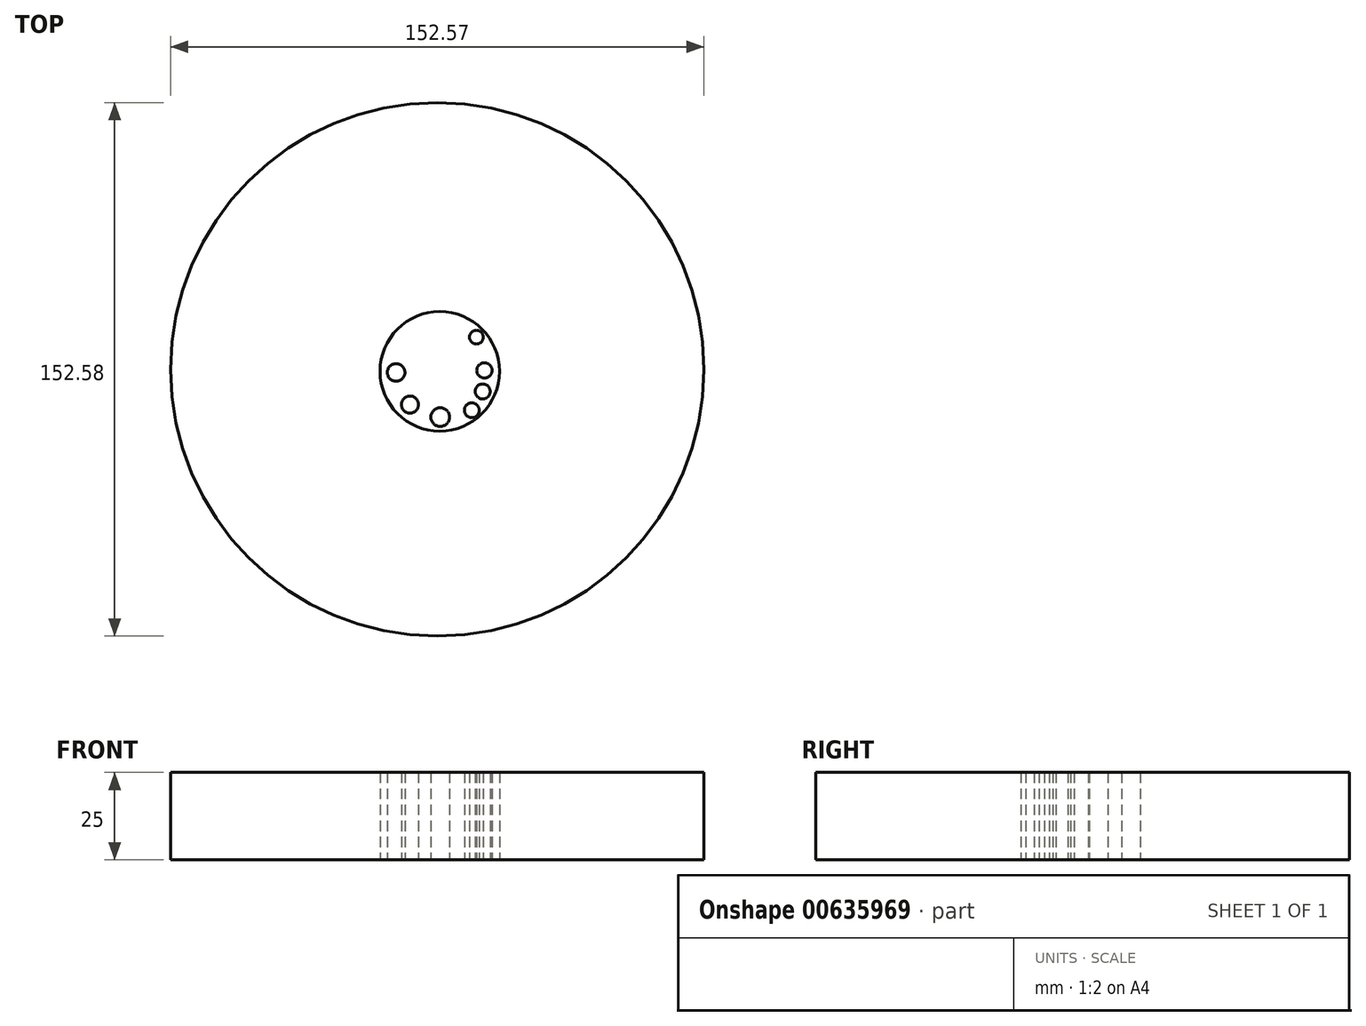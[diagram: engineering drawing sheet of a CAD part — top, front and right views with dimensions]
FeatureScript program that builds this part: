
annotation { "Feature Type Name" : "Feature", "Feature Type Description" : "" }
export const myFeature = defineFeature(function(context is Context, id is Id, definition is map)
    precondition{}
    {
        {
            var Q0;
            Q0=qCreatedBy(makeId("Top.planeOp"),FACE);
            var sketch = newSketch(context, id + "F0", { "sketchPlane" : qUnion([Q0])});
            skCircle(sketch, "E0", {"center": v(0, 0) * mm, "radius": 17.1 * mm});
            skSolve(sketch);
        }
        {
            var Q0;
            Q0=qCreatedBy(makeId("Top.planeOp"),FACE);
            var sketch = newSketch(context, id + "F1", { "sketchPlane" : qUnion([Q0])});
            skLineSegment(sketch, "E1", {"start": v(-13.82, 9.06) * mm, "end": v(-63.8, 0) * mm});
            skLineSegment(sketch, "E2", {"start": v(-63.8, 0) * mm, "end": v(-13.41, -6.4) * mm});
            skSolve(sketch);
        }
        {
            var Q0;
            Q0=qCreatedBy(makeId("Top.planeOp"),FACE);
            var sketch = newSketch(context, id + "F2", { "sketchPlane" : qUnion([Q0])});
            skLineSegment(sketch, "E3", {"start": v(15.18, 7.54) * mm, "end": v(64.83, 0) * mm});
            skLineSegment(sketch, "E4", {"start": v(64.83, 0) * mm, "end": v(16.7, -6.2) * mm});
            skSolve(sketch);
        }
        {
            var Q0;
            Q0=makeQuery(id+"F0.imprint","IMPRINT",FACE,{"disambiguationData":[TD([[makeQuery(id+"F0.imprint","IMPRINT",EDGE,{"derivedFrom":sQuery(id+"F0.wireOp",EDGE,"E0")}),1.0]])]});
            var sketch = newSketch(context, id + "F3", { "sketchPlane" : qUnion([Q0])});
            skCircle(sketch, "E5", {"center": v(-10.03, 9.26) * mm, "radius": 2.33 * mm});
            skSolve(sketch);
        }
        {
            var Q0;
            Q0=makeQuery(id+"F0.imprint","IMPRINT",FACE,{"disambiguationData":[TD([[makeQuery(id+"F0.imprint","IMPRINT",EDGE,{"derivedFrom":sQuery(id+"F0.wireOp",EDGE,"E0")}),1.0]])]});
            var sketch = newSketch(context, id + "F4", { "sketchPlane" : qUnion([Q0])});
            skCircle(sketch, "E6", {"center": v(0.3, 11.84) * mm, "radius": 2.4 * mm});
            skPoint(sketch, "E6.first.point", {"position": v(0, 9.45) * mm});
            skPoint(sketch, "E6.second.point", {"position": v(0, 14.23) * mm});
            skPoint(sketch, "E6.third.point", {"position": v(-2, 11.17) * mm});
            skSolve(sketch);
        }
        {
            var Q0;
            Q0=qCreatedBy(makeId("Top.planeOp"),FACE);
            var sketch = newSketch(context, id + "F5", { "sketchPlane" : qUnion([Q0])});
            skCircle(sketch, "E7", {"center": v(10.48, 9.79) * mm, "radius": 1.97 * mm});
            skPoint(sketch, "E7.first.point", {"position": v(9.83, 7.92) * mm});
            skPoint(sketch, "E7.second.point", {"position": v(10.22, 11.74) * mm});
            skPoint(sketch, "E7.third.point", {"position": v(9.07, 11.17) * mm});
            skCircle(sketch, "E8", {"center": v(-12.5, -0.32) * mm, "radius": 2.52 * mm});
            skPoint(sketch, "E8.first.point", {"position": v(-12.5, 2.2) * mm});
            skPoint(sketch, "E8.second.point", {"position": v(-13.08, -2.77) * mm});
            skPoint(sketch, "E8.third.point", {"position": v(-14.99, 0) * mm});
            skCircle(sketch, "E9", {"center": v(-8.52, -9.5) * mm, "radius": 2.44 * mm});
            skPoint(sketch, "E9.first.point", {"position": v(-7.35, -7.35) * mm});
            skPoint(sketch, "E9.second.point", {"position": v(-8.5, -11.93) * mm});
            skPoint(sketch, "E9.third.point", {"position": v(-10.79, -10.4) * mm});
            skCircle(sketch, "E10", {"center": v(0.12, -13.08) * mm, "radius": 2.68 * mm});
            skPoint(sketch, "E10.first.point", {"position": v(0, -10.4) * mm});
            skPoint(sketch, "E10.second.point", {"position": v(0, -15.75) * mm});
            skPoint(sketch, "E10.third.point", {"position": v(-2.2, -14.42) * mm});
            skCircle(sketch, "E11", {"center": v(9.17, -11.13) * mm, "radius": 2.13 * mm});
            skPoint(sketch, "E11.first.point", {"position": v(7.16, -10.4) * mm});
            skPoint(sketch, "E11.second.point", {"position": v(11.17, -10.4) * mm});
            skPoint(sketch, "E11.third.point", {"position": v(8.3, -13.08) * mm});
            skCircle(sketch, "E12", {"center": v(12.27, -5.76) * mm, "radius": 2.15 * mm});
            skPoint(sketch, "E12.first.point", {"position": v(10.4, -4.68) * mm});
            skPoint(sketch, "E12.second.point", {"position": v(14.42, -5.63) * mm});
            skPoint(sketch, "E12.third.point", {"position": v(13.84, -4.3) * mm});
            skCircle(sketch, "E13", {"center": v(12.77, 0.28) * mm, "radius": 2.2 * mm});
            skPoint(sketch, "E13.first.point", {"position": v(13.84, 2.2) * mm});
            skPoint(sketch, "E13.second.point", {"position": v(12.13, -1.81) * mm});
            skPoint(sketch, "E13.third.point", {"position": v(10.6, 0) * mm});
            skSolve(sketch);
        }
        {
            var Q0;
            Q0=qCreatedBy(makeId("Top.planeOp"),FACE);
            var sketch = newSketch(context, id + "F6", { "sketchPlane" : qUnion([Q0])});
            skCircle(sketch, "E14", {"center": v(-0.69, 0.57) * mm, "radius": 76.29 * mm});
            skPoint(sketch, "E14.first.point", {"position": v(0, 76.86) * mm});
            skPoint(sketch, "E14.second.point", {"position": v(0, -75.71) * mm});
            skPoint(sketch, "E14.third.point", {"position": v(-48.22, -59.1) * mm});
            skSolve(sketch);
        }
        {
            var Q0;
            Q0 = qSketchRegion(id + "F5", true);
            extrude(context, id + "F7", {"entities" : qUnion([Q0]), "depth" : 25 * mm, "offsetDistance" : 25 * mm});
        }
        {
            var Q0;
            Q0 = qSketchRegion(id + "F0", true);
            extrude(context, id + "F8", {"entities" : qUnion([Q0]), "depth" : 25 * mm, "offsetDistance" : 25 * mm});
        }
        {
            var Q0;
            Q0 = qSketchRegion(id + "F1", true);
            var Q1;
            Q1 = qSketchRegion(id + "F3", true);
            var Q2;
            Q2 = qSketchRegion(id + "F2", true);
            extrude(context, id + "F9", {"entities" : qUnion([Q0, Q1, Q2]), "operationType" : NewBodyOperationType.ADD, "depth" : 25 * mm, "offsetDistance" : 25 * mm});
        }
        {
            var Q0;
            Q0 = qSketchRegion(id + "F4", true);
            extrude(context, id + "F10", {"entities" : qUnion([Q0]), "operationType" : NewBodyOperationType.ADD, "depth" : 25 * mm, "offsetDistance" : 25 * mm});
        }
        {
            var Q0;
            Q0 = qSketchRegion(id + "F6", true);
            extrude(context, id + "F11", {"entities" : qUnion([Q0]), "depth" : 25 * mm, "offsetDistance" : 25 * mm});
        }
    });
